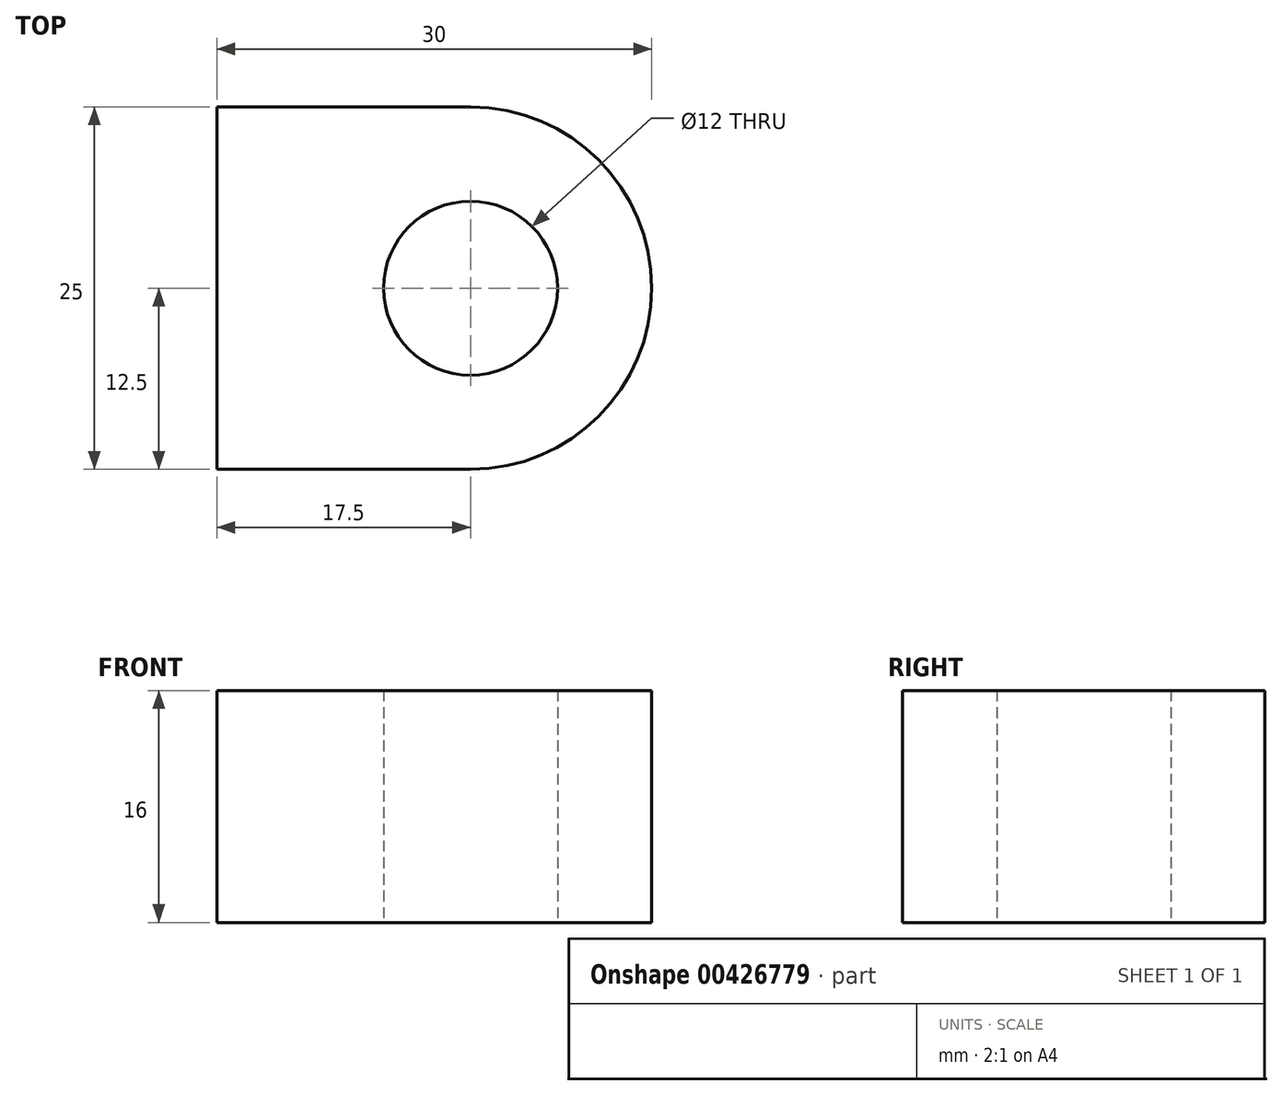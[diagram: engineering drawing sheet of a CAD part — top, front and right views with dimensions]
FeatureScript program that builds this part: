
annotation { "Feature Type Name" : "Feature", "Feature Type Description" : "" }
export const myFeature = defineFeature(function(context is Context, id is Id, definition is map)
    precondition{}
    {
        {
            var Q0;
            Q0=qCreatedBy(makeId("Top.planeOp"),FACE);
            var sketch = newSketch(context, id + "F0", { "sketchPlane" : qUnion([Q0])});
            skLineSegment(sketch, "E0.bottom", {"start": v(-17.5, 12.5) * mm, "end": v(12.5, 12.5) * mm});
            skLineSegment(sketch, "E0.top", {"start": v(-17.5, -12.5) * mm, "end": v(12.5, -12.5) * mm});
            skLineSegment(sketch, "E0.left", {"start": v(-17.5, 12.5) * mm, "end": v(-17.5, -12.5) * mm});
            skLineSegment(sketch, "E0.right", {"start": v(12.5, 12.5) * mm, "end": v(12.5, -12.5) * mm});
            skCircle(sketch, "E1", {"center": v(0, 0) * mm, "radius": 12.5 * mm});
            skPoint(sketch, "E1.centerSnap0", {"position": v(12.5, 0) * mm});
            skCircle(sketch, "E2", {"center": v(0, 0) * mm, "radius": 6 * mm});
            skSolve(sketch);
        }
        {
            var Q0;
            {var subQ0=sQuery(id+"F0.wireOp",EDGE,"E0.left");Q0=makeQuery(id+"F0.imprint","IMPRINT",FACE,{"disambiguationData":[TD([[makeQuery(id+"F0.imprint","IMPRINT",EDGE,{"derivedFrom":subQ0}),1.0]])]});}
            var Q1;
            Q1=makeQuery(id+"F0.imprint","IMPRINT",FACE,{"disambiguationData":[TD([[makeQuery(id+"F0.imprint","IMPRINT",EDGE,{"derivedFrom":sQuery(id+"F0.wireOp",EDGE,"E2")}),-1.0]])]});
            extrude(context, id + "F1", {"entities" : qUnion([Q0, Q1]), "depth" : 16 * mm});
        }
    });
